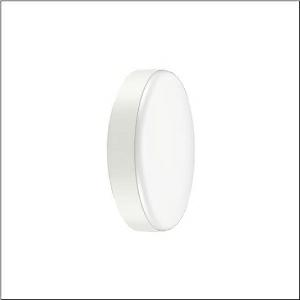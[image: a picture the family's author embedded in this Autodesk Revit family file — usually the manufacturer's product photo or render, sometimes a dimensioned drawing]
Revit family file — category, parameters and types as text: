
# Revit family: round_31_51wc10mb44as
name_source: partatom
category: Lighting Fixtures
units: mm (PartAtom-declared; Revit-internal decimal feet)

## family parameters
Cut with Voids When Loaded = No
Host = Face
Light Source = No
Part Type = Normal
Room Calculation Point = No
Round Connector Dimension = Use Diameter
Shared = No

## types (1)
- --- (1 x LED, 4400 lm, 35.5 W, 4000K)
    Apparent Load = 36 VA
    CIE Flux Codes = 44 75 94 94 100
    Color Rendering = 80
    Color Temperature = 4000K
    Default Elevation = 1800 mm
    Description = Round 31, wall and ceiling luminaire, primary optical cover: cover, of PC, opal, light emission: direct distribution, primary light characteristic: symmetric, installation type: surface-mounted, LED, rated luminous flux: 4.400lm, luminous efficacy: 124lm/W, light colour: 840, colour temperature: 4000K, control gear: ON/OFF Multilumen, with terminal, 3-pole, max. 2.5mm², mains connection: 220..240V, AC, 50/60Hz, rated input power: 35.5W, luminaire housing, of PC, traffic white (RAL 9016), diameter: 480mm, brightness and presence sensor, HF sensor, protection rating (complete): IP65, insulation class (complete): insulation class II (safety insulation), certification: CE, impact resistance: IK10, permissible operating ambient temperature: -20..+40°C, permissible storage temperature: -20..+60°C, packaging unit: 1 piece
    Height = 97 mm
    Lamp = 1 x LED
    Lamp Light Flux = 4400 lm
    Lamp Power = 35.5 W
    Lamp count = 1
    Length = 480 mm
    Luminous efficacy = 124 lm/W
    Manufacturer = Siteco
    ModVariant = No
    Model = 51WC10MB44AS
    Mounting Place = Wall
    Mounting Type = Surface mounted
    Number of Poles = 1
    OnlyDefault = Yes
    Power Factor = 1
    Product Name = Round 31
    Product group = wall and ceiling luminaire | wall mounted
    ProductGroupID = 2001
    Protection Class = Protection class II
    Protection Degree = IP 65
    RLX_Detail_Level = 1
    RLX_Emergency_Light_Flux = 0 lm
    RLX_Emergency_Type = 0
    RLX_Emergency_Type_DB = No
    RlxData = <blob elided: 41493 chars, md5=cb5abde1>
    Socket = socket
    Standby Power = 0 W
    System Light Flux = 4400 lm
    System Power = 36 W
    Type Comments = factory setting: luminous flux: 100 % | (ON | ON)
    Type Image = l_1007188.jpg
    URL = http://relux.com
    VarID = @adj_150285
    Voltage = 0 V
    Weight = 0.00 kg
    Width = 0 mm  [stored 0 ft]

note: [stored X ft] marks values corroborated as IEEE doubles in the binary element streams (Revit-internal decimal feet)

## geometry (parser evidence)
native form markers: Blend x4, Sweep x13
no freeform markers — native parametric forms only
